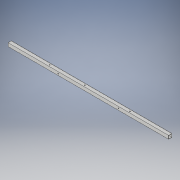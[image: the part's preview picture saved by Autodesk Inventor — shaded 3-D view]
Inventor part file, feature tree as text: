
AUTODESK INVENTOR PART (.ipt)
format: ipt  version: 2017 (Build 210142000, 142)  size: 126,976 bytes
history: native  units: in
note: dims shown in document units (in); Inventor stores cm internally (conversion verified against a paired STEP export)
features: extrude x3, sketch x3
ambient origin geometry x8: Origin, YZ Plane, XZ Plane, XY Plane, X Axis, Y Axis, Z Axis, Center Point
bodies: Solid1 (feature_tree)
feature tree (6):
  extrude  "Extrusion1"  Depth=1.0in
  extrude  "Extrusion3"  Depth=48.0in TaperAngle=0.0deg
  extrude  "Extrusion4"  Depth=1.0in
  sketch  "Sketch1"  dims[d0=1.0in d1=1.0in]
  sketch  "Sketch3"  dims[d2=0.0625in d3=48.0in d4=0.0in]
  sketch  "Sketch4"  dims[d10=0.25in d11=12.0in d12=1.0in d13=0.0in d14=1.5in d15=0.25in d17=1.0in d18=0.0in d19=9.0in]
